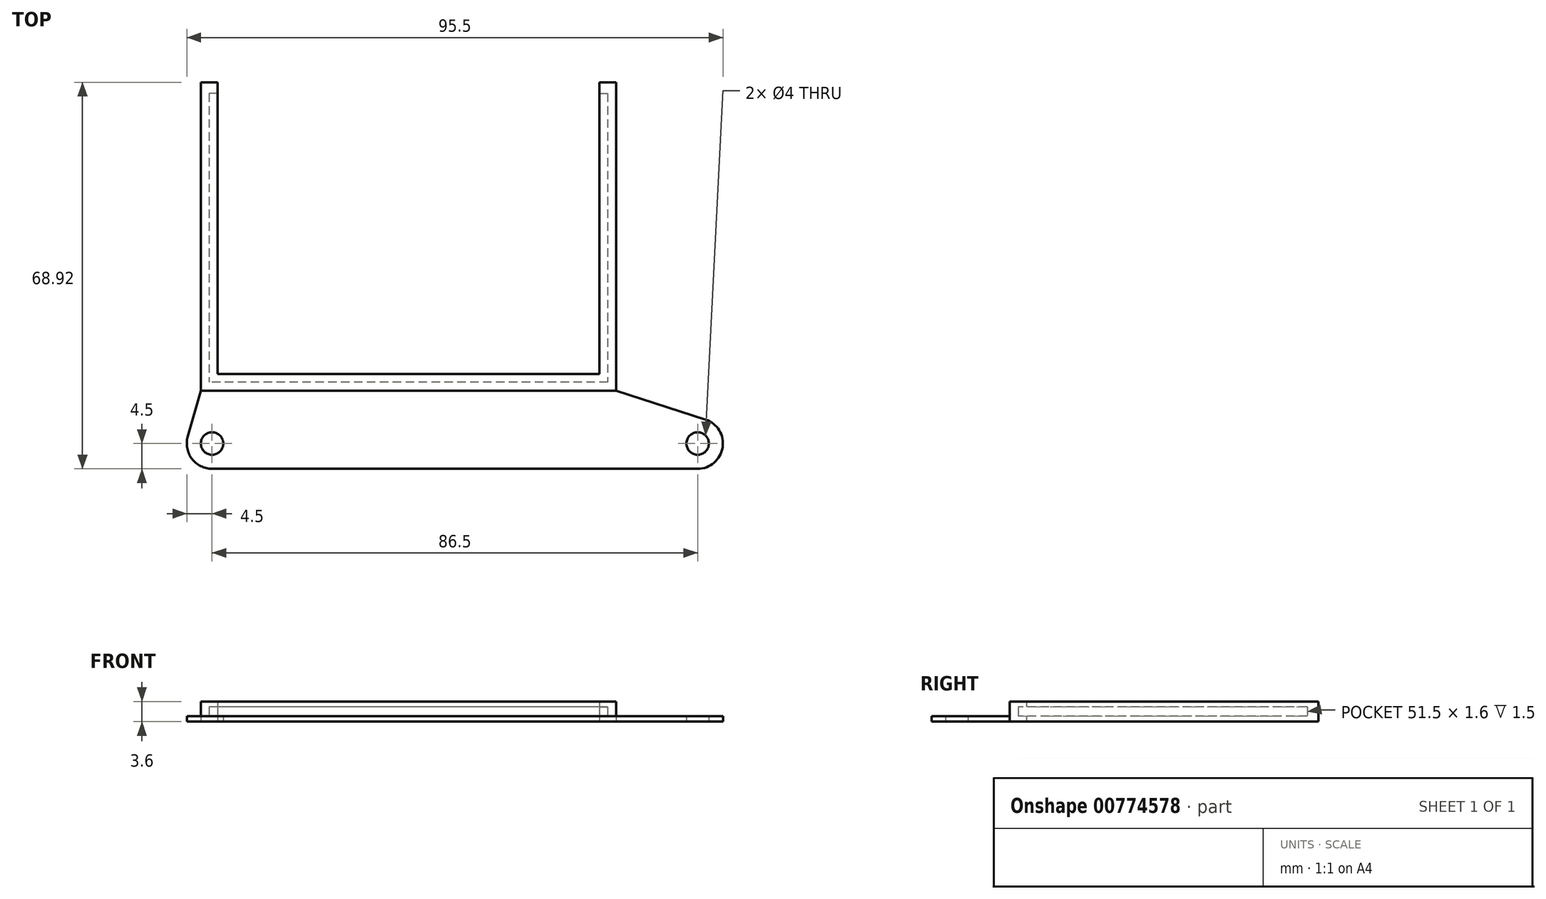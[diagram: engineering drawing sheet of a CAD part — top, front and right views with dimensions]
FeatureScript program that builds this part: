
annotation { "Feature Type Name" : "Feature", "Feature Type Description" : "" }
export const myFeature = defineFeature(function(context is Context, id is Id, definition is map)
    precondition{}
    {
        {
            var Q0;
            Q0=qCreatedBy(makeId("Top.planeOp"),FACE);
            var sketch = newSketch(context, id + "F0", { "sketchPlane" : qUnion([Q0])});
            skLineSegment(sketch, "E0", {"start": v(-27, -33.5) * mm, "end": v(52.5, -33.5) * mm, "construction": true});
            skCircle(sketch, "E1", {"center": v(-30.5, -33.5) * mm, "radius": 3.5 * mm, "construction": true});
            skCircle(sketch, "E2", {"center": v(56, -33.5) * mm, "radius": 3.5 * mm, "construction": true});
            skLineSegment(sketch, "E3", {"start": v(-35, -29) * mm, "end": v(60.5, -29) * mm, "construction": true});
            skLineSegment(sketch, "E4", {"start": v(60.5, -29) * mm, "end": v(60.5, -38) * mm, "construction": true});
            skLineSegment(sketch, "E5", {"start": v(60.5, -38) * mm, "end": v(-35, -38) * mm, "construction": true});
            skLineSegment(sketch, "E6", {"start": v(-35, -38) * mm, "end": v(-35, -29) * mm, "construction": true});
            skLineSegment(sketch, "E7", {"start": v(12.75, -23.41) * mm, "end": v(12.75, -44.43) * mm, "construction": true});
            skSolve(sketch);
        }
        {
            var Q0;
            Q0=qCreatedBy(makeId("Top.planeOp"),FACE);
            var sketch = newSketch(context, id + "F1", { "sketchPlane" : qUnion([Q0])});
            skCircle(sketch, "E8", {"center": v(-30.5, -33.5) * mm, "radius": 4.5 * mm});
            skLineSegment(sketch, "E9", {"start": v(-34.83, -32.28) * mm, "end": v(-32.51, -24.08) * mm});
            skCircle(sketch, "E10", {"center": v(56, -33.5) * mm, "radius": 4.5 * mm});
            skLineSegment(sketch, "E11", {"start": v(57.38, -29.22) * mm, "end": v(41.49, -24.08) * mm});
            skLineSegment(sketch, "E12.bottom", {"start": v(-30.51, 27.92) * mm, "end": v(39.49, 27.92) * mm, "construction": true});
            skLineSegment(sketch, "E12.top", {"start": v(-30.51, -22.08) * mm, "end": v(39.49, -22.08) * mm, "construction": true});
            skLineSegment(sketch, "E12.left", {"start": v(-30.51, 27.92) * mm, "end": v(-30.51, -22.08) * mm, "construction": true});
            skLineSegment(sketch, "E12.right", {"start": v(39.49, 27.92) * mm, "end": v(39.49, -22.08) * mm, "construction": true});
            skLineSegment(sketch, "E13", {"start": v(-30.5, -38) * mm, "end": v(56, -38) * mm});
            skLineSegment(sketch, "E14", {"start": v(-32.51, 27.92) * mm, "end": v(-32.51, -24.08) * mm});
            skLineSegment(sketch, "E15", {"start": v(-32.51, -24.08) * mm, "end": v(41.49, -24.08) * mm});
            skLineSegment(sketch, "E16", {"start": v(41.49, -24.08) * mm, "end": v(41.49, 27.92) * mm});
            skLineSegment(sketch, "E17", {"start": v(-32.51, 27.92) * mm, "end": v(-29.51, 27.92) * mm});
            skLineSegment(sketch, "E18", {"start": v(-29.51, 27.92) * mm, "end": v(-29.51, -21.08) * mm});
            skLineSegment(sketch, "E19", {"start": v(-29.51, -21.08) * mm, "end": v(38.49, -21.08) * mm});
            skLineSegment(sketch, "E20", {"start": v(38.49, -21.08) * mm, "end": v(38.49, 27.92) * mm});
            skLineSegment(sketch, "E21", {"start": v(38.49, 27.92) * mm, "end": v(41.49, 27.92) * mm});
            skLineSegment(sketch, "E22", {"start": v(4.49, 17.06) * mm, "end": v(4.49, -6.03) * mm, "construction": true});
            skCircle(sketch, "E23", {"center": v(-30.5, -33.5) * mm, "radius": 2 * mm});
            skCircle(sketch, "E24", {"center": v(56, -33.5) * mm, "radius": 2 * mm});
            skLineSegment(sketch, "E25", {"start": v(-32.51, 27.92) * mm, "end": v(-32.51, 30.92) * mm});
            skLineSegment(sketch, "E26", {"start": v(-32.51, 30.92) * mm, "end": v(-29.51, 30.92) * mm});
            skLineSegment(sketch, "E27", {"start": v(-29.51, 30.92) * mm, "end": v(-29.51, 27.92) * mm});
            skLineSegment(sketch, "E28.MirrorCS", {"start": v(41.49, 27.92) * mm, "end": v(41.49, 30.92) * mm});
            skLineSegment(sketch, "E29.MirrorCS", {"start": v(41.49, 30.92) * mm, "end": v(38.49, 30.92) * mm});
            skLineSegment(sketch, "E30.MirrorCS", {"start": v(38.49, 30.92) * mm, "end": v(38.49, 27.92) * mm});
            skSolve(sketch);
        }
        {
            var Q0;
            Q0=qCreatedBy(makeId("Top.planeOp"),FACE);
            cPlane(context, id + "F2", {"entities" : qUnion([Q0]), "cplaneType" : CPlaneType.OFFSET, "offset" : 1 * mm, "width" : 150 * mm, "height" : 150 * mm});
        }
        {
            var Q0;
            Q0=qCreatedBy(id+"F2.planeOp",FACE);
            var sketch = newSketch(context, id + "F3", { "sketchPlane" : qUnion([Q0])});
            skLineSegment(sketch, "E31", {"start": v(-32.51, 27.92) * mm, "end": v(-32.51, -24.08) * mm});
            skLineSegment(sketch, "E32", {"start": v(-32.51, -24.08) * mm, "end": v(41.49, -24.08) * mm});
            skLineSegment(sketch, "E33", {"start": v(41.49, -24.08) * mm, "end": v(41.49, 27.92) * mm});
            skLineSegment(sketch, "E34", {"start": v(41.49, 27.92) * mm, "end": v(39.99, 27.92) * mm});
            skLineSegment(sketch, "E35", {"start": v(39.99, 27.92) * mm, "end": v(39.99, -22.58) * mm});
            skLineSegment(sketch, "E36", {"start": v(39.99, -22.58) * mm, "end": v(-31.01, -22.58) * mm});
            skLineSegment(sketch, "E37", {"start": v(-31.01, -22.58) * mm, "end": v(-31.01, 27.92) * mm});
            skLineSegment(sketch, "E38", {"start": v(-31.01, 27.92) * mm, "end": v(-32.51, 27.92) * mm});
            skLineSegment(sketch, "E39", {"start": v(-32.51, 27.92) * mm, "end": v(-32.51, 30.92) * mm});
            skLineSegment(sketch, "E40", {"start": v(-32.51, 30.92) * mm, "end": v(-29.51, 30.92) * mm});
            skLineSegment(sketch, "E41", {"start": v(-29.51, 30.92) * mm, "end": v(-29.51, 28.92) * mm});
            skLineSegment(sketch, "E42", {"start": v(-29.51, 28.92) * mm, "end": v(-31.01, 28.92) * mm});
            skLineSegment(sketch, "E43", {"start": v(-31.01, 28.92) * mm, "end": v(-31.01, 27.92) * mm});
            skLineSegment(sketch, "E44.MirrorCS", {"start": v(39.99, 28.92) * mm, "end": v(39.99, 27.92) * mm});
            skLineSegment(sketch, "E45.MirrorCS", {"start": v(38.49, 28.92) * mm, "end": v(39.99, 28.92) * mm});
            skLineSegment(sketch, "E46.MirrorCS", {"start": v(38.49, 30.92) * mm, "end": v(38.49, 28.92) * mm});
            skLineSegment(sketch, "E47.MirrorCS", {"start": v(41.49, 30.92) * mm, "end": v(38.49, 30.92) * mm});
            skLineSegment(sketch, "E48.MirrorCS", {"start": v(41.49, 27.92) * mm, "end": v(41.49, 30.92) * mm});
            skSolve(sketch);
        }
        {
            var Q0;
            Q0=qCreatedBy(id+"F2.planeOp",FACE);
            cPlane(context, id + "F4", {"entities" : qUnion([Q0]), "cplaneType" : CPlaneType.OFFSET, "offset" : 1.6 * mm, "width" : 150 * mm, "height" : 150 * mm});
        }
        {
            var Q0;
            Q0=qCreatedBy(id+"F4.planeOp",FACE);
            var sketch = newSketch(context, id + "F5", { "sketchPlane" : qUnion([Q0])});
            skLineSegment(sketch, "E49", {"start": v(-32.51, 27.92) * mm, "end": v(-32.51, -24.08) * mm});
            skLineSegment(sketch, "E50", {"start": v(-32.51, -24.08) * mm, "end": v(41.49, -24.08) * mm});
            skLineSegment(sketch, "E51", {"start": v(41.49, -24.08) * mm, "end": v(41.49, 27.92) * mm});
            skLineSegment(sketch, "E52", {"start": v(41.49, 27.92) * mm, "end": v(38.49, 27.92) * mm});
            skLineSegment(sketch, "E53", {"start": v(38.49, 27.92) * mm, "end": v(38.49, -21.08) * mm});
            skLineSegment(sketch, "E54", {"start": v(38.49, -21.08) * mm, "end": v(-29.51, -21.08) * mm});
            skLineSegment(sketch, "E55", {"start": v(-29.51, -21.08) * mm, "end": v(-29.51, 27.92) * mm});
            skLineSegment(sketch, "E56", {"start": v(-29.51, 27.92) * mm, "end": v(-32.51, 27.92) * mm});
            skLineSegment(sketch, "E57", {"start": v(-32.51, 27.92) * mm, "end": v(-32.51, 30.92) * mm});
            skLineSegment(sketch, "E58", {"start": v(-32.51, 30.92) * mm, "end": v(-29.51, 30.92) * mm});
            skLineSegment(sketch, "E59", {"start": v(-29.51, 30.92) * mm, "end": v(-29.51, 27.92) * mm});
            skLineSegment(sketch, "E60.MirrorCS", {"start": v(38.49, 30.92) * mm, "end": v(38.49, 27.92) * mm});
            skLineSegment(sketch, "E61.MirrorCS", {"start": v(41.49, 27.92) * mm, "end": v(41.49, 30.92) * mm});
            skLineSegment(sketch, "E62.MirrorCS", {"start": v(41.49, 30.92) * mm, "end": v(38.49, 30.92) * mm});
            skSolve(sketch);
        }
        {
            var Q0;
            Q0 = qSketchRegion(id + "F1", true);
            var Q1;
            Q1=qCreatedBy(id+"F2.planeOp",FACE);
            extrude(context, id + "F6", {"entities" : qUnion([Q0]), "endBound" : BoundingType.UP_TO_SURFACE, "depth" : 25 * mm, "endBoundEntityFace" : qUnion([Q1]), "offsetDistance" : 25 * mm});
        }
        {
            var Q0;
            Q0 = qSketchRegion(id + "F3", true);
            var Q1;
            Q1=qCreatedBy(id+"F4.planeOp",FACE);
            extrude(context, id + "F7", {"entities" : qUnion([Q0]), "operationType" : NewBodyOperationType.ADD, "endBound" : BoundingType.UP_TO_SURFACE, "depth" : 25 * mm, "endBoundEntityFace" : qUnion([Q1]), "offsetDistance" : 25 * mm});
        }
        {
            var Q0;
            Q0 = qSketchRegion(id + "F5", true);
            extrude(context, id + "F8", {"entities" : qUnion([Q0]), "operationType" : NewBodyOperationType.ADD, "depth" : 1 * mm, "offsetDistance" : 25 * mm});
        }
    });
